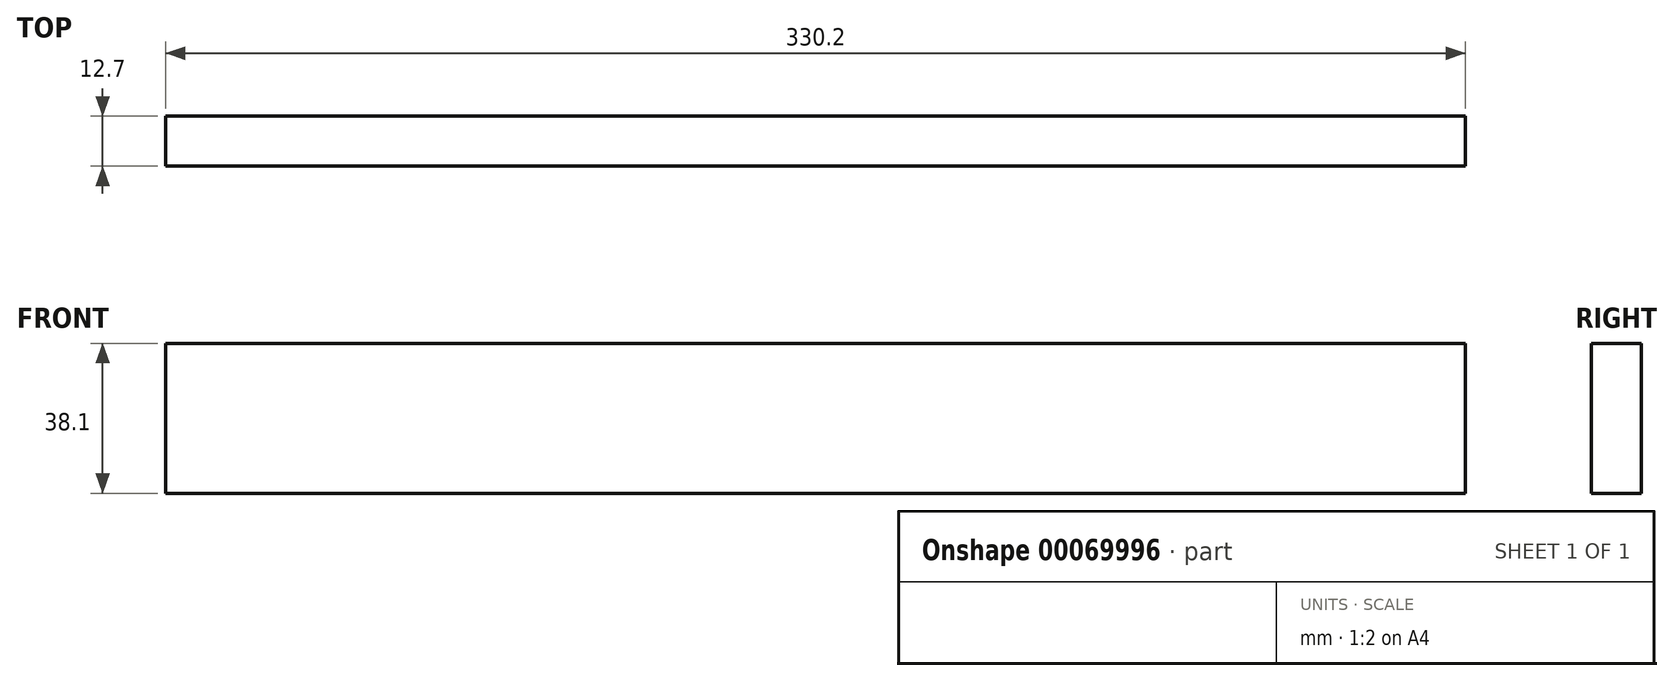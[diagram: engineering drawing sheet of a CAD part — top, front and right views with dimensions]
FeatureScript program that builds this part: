
annotation { "Feature Type Name" : "Feature", "Feature Type Description" : "" }
export const myFeature = defineFeature(function(context is Context, id is Id, definition is map)
    precondition{}
    {
        {
            var Q0;
            Q0=qCreatedBy(makeId("Front.planeOp"),FACE);
            var sketch = newSketch(context, id + "F0", { "sketchPlane" : qUnion([Q0])});
            skLineSegment(sketch, "E0.rect.bottom", {"start": v(165.1, 19.05) * mm, "end": v(-165.1, 19.05) * mm});
            skLineSegment(sketch, "E0.rect.top", {"start": v(165.1, -19.05) * mm, "end": v(-165.1, -19.05) * mm});
            skLineSegment(sketch, "E0.rect.left", {"start": v(165.1, 19.05) * mm, "end": v(165.1, -19.05) * mm});
            skLineSegment(sketch, "E0.rect.right", {"start": v(-165.1, 19.05) * mm, "end": v(-165.1, -19.05) * mm});
            skPoint(sketch, "E0.rect.middle", {"position": v(0, 0) * mm});
            skLineSegment(sketch, "E1", {"start": v(0, 19.05) * mm, "end": v(0, -19.05) * mm, "construction": true});
            skSolve(sketch);
        }
        {
            var Q0;
            Q0=makeQuery(id+"F0.imprint","IMPRINT",FACE,{"disambiguationData":[TD([[makeQuery(id+"F0.imprint","IMPRINT",EDGE,{"derivedFrom":sQuery(id+"F0.wireOp",EDGE,"abd1e121-c28f-4105-937f-708772ba65bf.bottom")}),1.0]])]});
            var Q1;
            {var subQ3=sQuery(id+"F0.wireOp",EDGE,"E0.rect.bottom");Q1=makeQuery(id+"F0.imprint","IMPRINT",FACE,{"disambiguationData":[TD([[makeQuery(id+"F0.imprint","IMPRINT",EDGE,{"derivedFrom":subQ3}),1.0]])]});}
            var Q2;
            Q2=makeQuery(id+"F0.imprint","IMPRINT",FACE,{"disambiguationData":[TD([[makeQuery(id+"F0.imprint","IMPRINT",EDGE,{"derivedFrom":sQuery(id+"F0.wireOp",EDGE,"98e05f21-933e-4f51-9880-0251b27cb64b0.MirrorCS")}),-1.0]])]});
            extrude(context, id + "F1", {"entities" : qUnion([Q0, Q1, Q2]), "depth" : 12.7 * mm});
        }
    });
